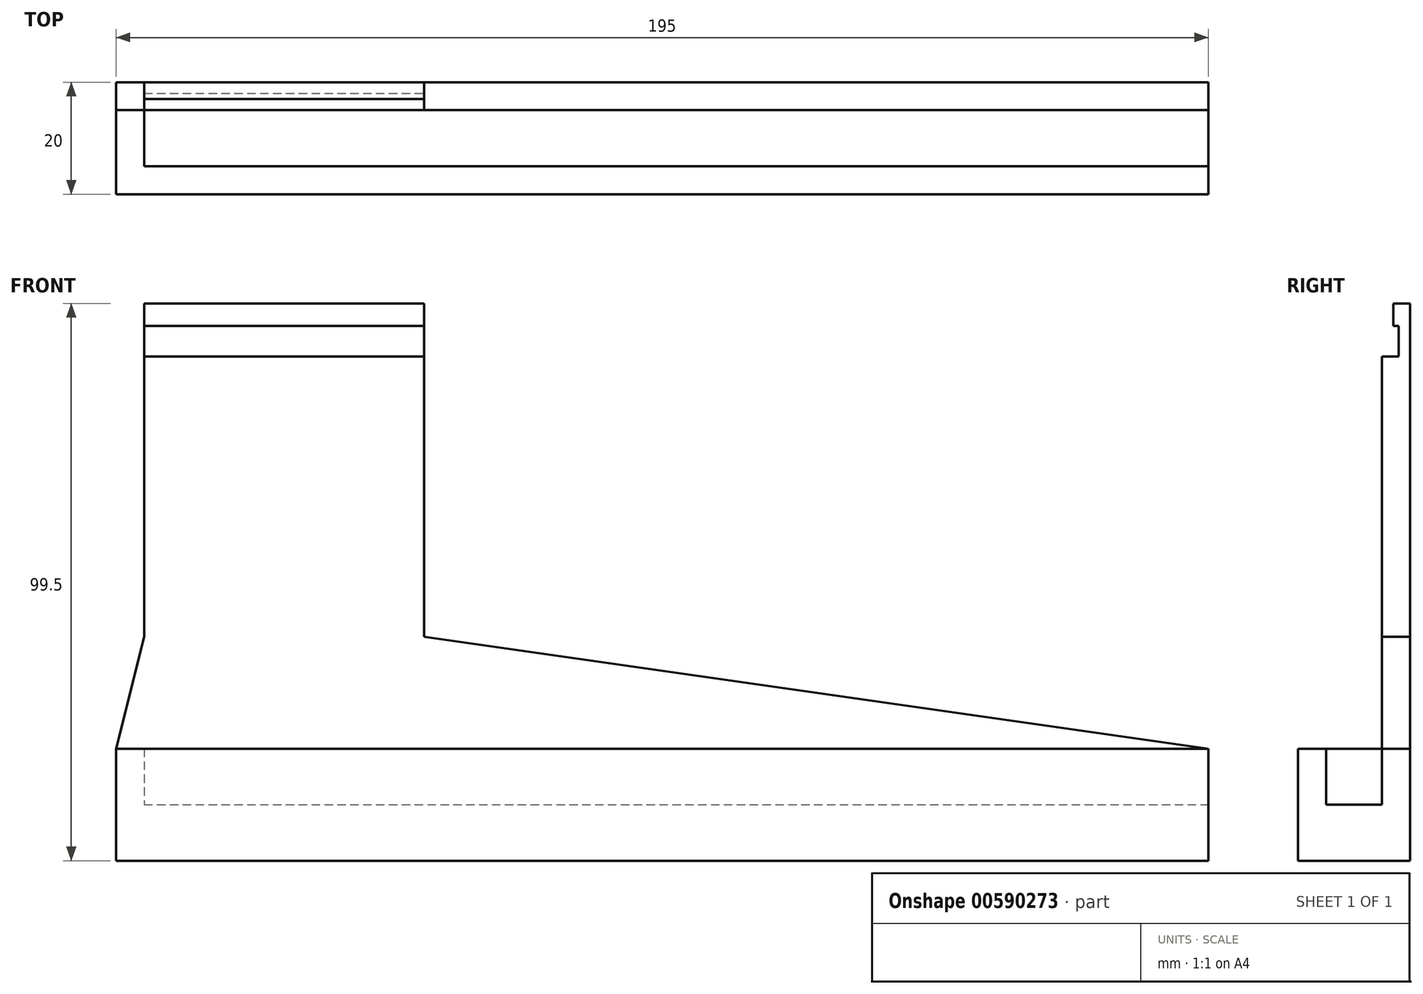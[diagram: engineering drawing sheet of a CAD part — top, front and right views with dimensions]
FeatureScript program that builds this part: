
annotation { "Feature Type Name" : "Feature", "Feature Type Description" : "" }
export const myFeature = defineFeature(function(context is Context, id is Id, definition is map)
    precondition{}
    {
        {
            var Q0;
            Q0=qCreatedBy(makeId("Top.planeOp"),FACE);
            var sketch = newSketch(context, id + "F0", { "sketchPlane" : qUnion([Q0])});
            skLineSegment(sketch, "E0.bottom", {"start": v(0, 0) * mm, "end": v(5, 0) * mm});
            skLineSegment(sketch, "E0.top", {"start": v(0, 20) * mm, "end": v(5, 20) * mm});
            skLineSegment(sketch, "E0.left", {"start": v(0, 0) * mm, "end": v(0, 20) * mm});
            skLineSegment(sketch, "E0.right", {"start": v(5, 0) * mm, "end": v(5, 20) * mm});
            skLineSegment(sketch, "E1.bottom", {"start": v(5, 20) * mm, "end": v(195, 20) * mm});
            skLineSegment(sketch, "E1.top", {"start": v(5, 15) * mm, "end": v(195, 15) * mm});
            skLineSegment(sketch, "E1.left", {"start": v(5, 20) * mm, "end": v(5, 15) * mm});
            skLineSegment(sketch, "E1.right", {"start": v(195, 20) * mm, "end": v(195, 15) * mm});
            skLineSegment(sketch, "E2.bottom", {"start": v(5, 0) * mm, "end": v(195, 0) * mm});
            skLineSegment(sketch, "E2.top", {"start": v(5, 5) * mm, "end": v(195, 5) * mm});
            skLineSegment(sketch, "E2.left", {"start": v(5, 0) * mm, "end": v(5, 5) * mm});
            skLineSegment(sketch, "E2.right", {"start": v(195, 0) * mm, "end": v(195, 5) * mm});
            skSolve(sketch);
        }
        {
            var Q0;
            Q0 = qSketchRegion(id + "F0", true);
            extrude(context, id + "F1", {"entities" : qUnion([Q0]), "depth" : 20 * mm, "offsetDistance" : 25 * mm});
        }
        {
            var Q0;
            Q0=qCreatedBy(makeId("Top.planeOp"),FACE);
            var sketch = newSketch(context, id + "F2", { "sketchPlane" : qUnion([Q0])});
            skLineSegment(sketch, "E3.bottom", {"start": v(5, 5) * mm, "end": v(195, 5) * mm});
            skLineSegment(sketch, "E3.top", {"start": v(5, 15) * mm, "end": v(195, 15) * mm});
            skLineSegment(sketch, "E3.left", {"start": v(5, 5) * mm, "end": v(5, 15) * mm});
            skLineSegment(sketch, "E3.right", {"start": v(195, 5) * mm, "end": v(195, 15) * mm});
            skSolve(sketch);
        }
        {
            var Q0;
            Q0 = qSketchRegion(id + "F2", true);
            extrude(context, id + "F3", {"entities" : qUnion([Q0]), "operationType" : NewBodyOperationType.ADD, "depth" : 10 * mm, "offsetDistance" : 25 * mm});
        }
        {
            var Q0;
            Q0=makeQuery(id+"F1.opExtrude","CAP_FACE",FACE,{"disambiguationData":[OSD([sQuery(id+"F0.wireOp",EDGE,"E0.bottom"),sQuery(id+"F0.wireOp",EDGE,"E0.top"),sQuery(id+"F0.wireOp",EDGE,"E0.left"),sQuery(id+"F0.wireOp",EDGE,"E0.right"),sQuery(id+"F0.wireOp",EDGE,"E1.bottom"),sQuery(id+"F0.wireOp",EDGE,"E1.top"),sQuery(id+"F0.wireOp",EDGE,"E1.right"),sQuery(id+"F0.wireOp",EDGE,"E2.bottom"),sQuery(id+"F0.wireOp",EDGE,"E2.top"),sQuery(id+"F0.wireOp",EDGE,"E2.right")])],"isStart":false});
            var sketch = newSketch(context, id + "F4", { "sketchPlane" : qUnion([Q0])});
            skLineSegment(sketch, "E4.bottom", {"start": v(5, 20) * mm, "end": v(55, 20) * mm});
            skLineSegment(sketch, "E4.top", {"start": v(5, 15) * mm, "end": v(55, 15) * mm});
            skLineSegment(sketch, "E4.left", {"start": v(5, 20) * mm, "end": v(5, 15) * mm});
            skLineSegment(sketch, "E4.right", {"start": v(55, 20) * mm, "end": v(55, 15) * mm});
            skSolve(sketch);
        }
        {
            var Q0;
            Q0 = qSketchRegion(id + "F4", true);
            extrude(context, id + "F5", {"entities" : qUnion([Q0]), "operationType" : NewBodyOperationType.ADD, "depth" : 70 * mm, "offsetDistance" : 25 * mm});
        }
        {
            var Q0;
            Q0=makeQuery(id+"F5.boolean.opBoolean","MERGE",FACE,{"derivedFrom":[makeQuery(id+"F1.opExtrude","SWEPT_FACE",FACE,{"disambiguationData":[OSD([sQuery(id+"F0.wireOp",EDGE,"E0.top"),sQuery(id+"F0.wireOp",EDGE,"E1.bottom")])]}),makeQuery(id+"F5.opExtrude","SWEPT_FACE",FACE,{"disambiguationData":[OSD([sQuery(id+"F4.wireOp",EDGE,"E4.bottom")])]})]});
            var sketch = newSketch(context, id + "F6", { "sketchPlane" : qUnion([Q0])});
            skLineSegment(sketch, "E5", {"start": v(0, 20) * mm, "end": v(-5, 20) * mm});
            skLineSegment(sketch, "E6", {"start": v(-5, 20) * mm, "end": v(-5, 40) * mm});
            skLineSegment(sketch, "E7", {"start": v(-5, 40) * mm, "end": v(0, 20) * mm});
            skLineSegment(sketch, "E8", {"start": v(-55, 20) * mm, "end": v(-195, 20) * mm});
            skLineSegment(sketch, "E9", {"start": v(-195, 20) * mm, "end": v(-55, 40) * mm});
            skLineSegment(sketch, "E10", {"start": v(-55, 40) * mm, "end": v(-55, 20) * mm});
            skSolve(sketch);
        }
        {
            var Q0;
            Q0 = qSketchRegion(id + "F6", true);
            extrude(context, id + "F7", {"entities" : qUnion([Q0]), "operationType" : NewBodyOperationType.ADD, "oppositeDirection" : true, "depth" : 5 * mm, "offsetDistance" : 25 * mm});
        }
        {
            var Q0;
            Q0=makeQuery(id+"F5.opExtrude","CAP_FACE",FACE,{"disambiguationData":[OSD([sQuery(id+"F4.wireOp",EDGE,"E4.bottom"),sQuery(id+"F4.wireOp",EDGE,"E4.top"),sQuery(id+"F4.wireOp",EDGE,"E4.left"),sQuery(id+"F4.wireOp",EDGE,"E4.right")])],"isStart":false});
            var sketch = newSketch(context, id + "F8", { "sketchPlane" : qUnion([Q0])});
            skLineSegment(sketch, "E11.bottom", {"start": v(5, 20) * mm, "end": v(55, 20) * mm});
            skLineSegment(sketch, "E11.top", {"start": v(5, 18) * mm, "end": v(55, 18) * mm});
            skLineSegment(sketch, "E11.left", {"start": v(5, 20) * mm, "end": v(5, 18) * mm});
            skLineSegment(sketch, "E11.right", {"start": v(55, 20) * mm, "end": v(55, 18) * mm});
            skSolve(sketch);
        }
        {
            var Q0;
            Q0 = qSketchRegion(id + "F8", true);
            extrude(context, id + "F9", {"entities" : qUnion([Q0]), "operationType" : NewBodyOperationType.ADD, "depth" : 5.5 * mm, "offsetDistance" : 25 * mm});
        }
        {
            var Q0;
            Q0=makeQuery(id+"F9.opExtrude","CAP_FACE",FACE,{"disambiguationData":[OSD([sQuery(id+"F8.wireOp",EDGE,"E11.bottom"),sQuery(id+"F8.wireOp",EDGE,"E11.top"),sQuery(id+"F8.wireOp",EDGE,"E11.left"),sQuery(id+"F8.wireOp",EDGE,"E11.right")])],"isStart":false});
            var sketch = newSketch(context, id + "F10", { "sketchPlane" : qUnion([Q0])});
            skLineSegment(sketch, "E12.bottom", {"start": v(5, 20) * mm, "end": v(55, 20) * mm});
            skLineSegment(sketch, "E12.top", {"start": v(5, 17) * mm, "end": v(55, 17) * mm});
            skLineSegment(sketch, "E12.left", {"start": v(5, 20) * mm, "end": v(5, 17) * mm});
            skLineSegment(sketch, "E12.right", {"start": v(55, 20) * mm, "end": v(55, 17) * mm});
            skSolve(sketch);
        }
        {
            var Q0;
            Q0 = qSketchRegion(id + "F10", true);
            extrude(context, id + "F11", {"entities" : qUnion([Q0]), "operationType" : NewBodyOperationType.ADD, "depth" : 4 * mm, "offsetDistance" : 25 * mm});
        }
    });
